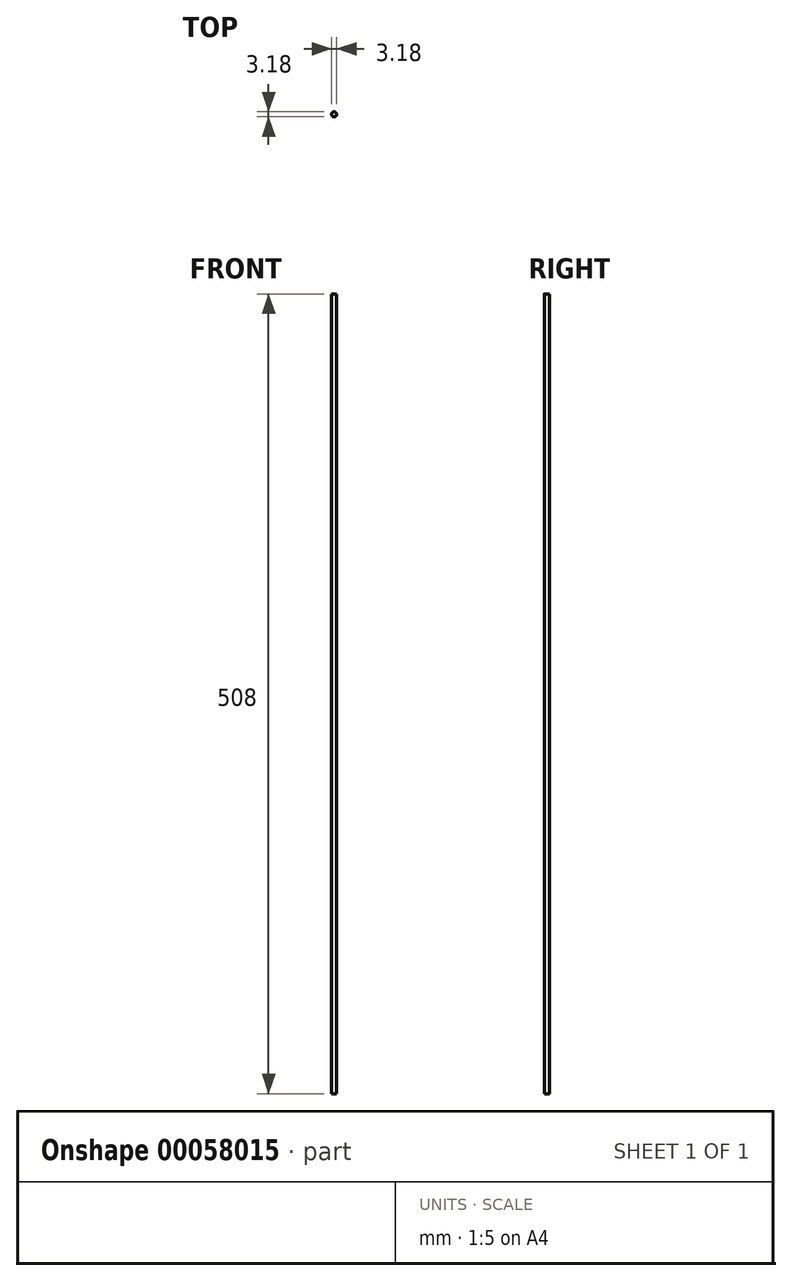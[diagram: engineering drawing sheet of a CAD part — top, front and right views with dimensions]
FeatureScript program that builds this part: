
annotation { "Feature Type Name" : "Feature", "Feature Type Description" : "" }
export const myFeature = defineFeature(function(context is Context, id is Id, definition is map)
    precondition{}
    {
        {
            var Q0;
            Q0=qCreatedBy(makeId("Top.planeOp"),FACE);
            var sketch = newSketch(context, id + "F0", { "sketchPlane" : qUnion([Q0])});
            skCircle(sketch, "E0", {"center": v(0, 0) * mm, "radius": 1.59 * mm});
            skSolve(sketch);
        }
        {
            var Q0;
            Q0=qSketchRegion(id+"F0",true);
            extrude(context, id + "F1", {"entities" : qUnion([Q0]), "depth" : 508 * mm});
        }
    });
